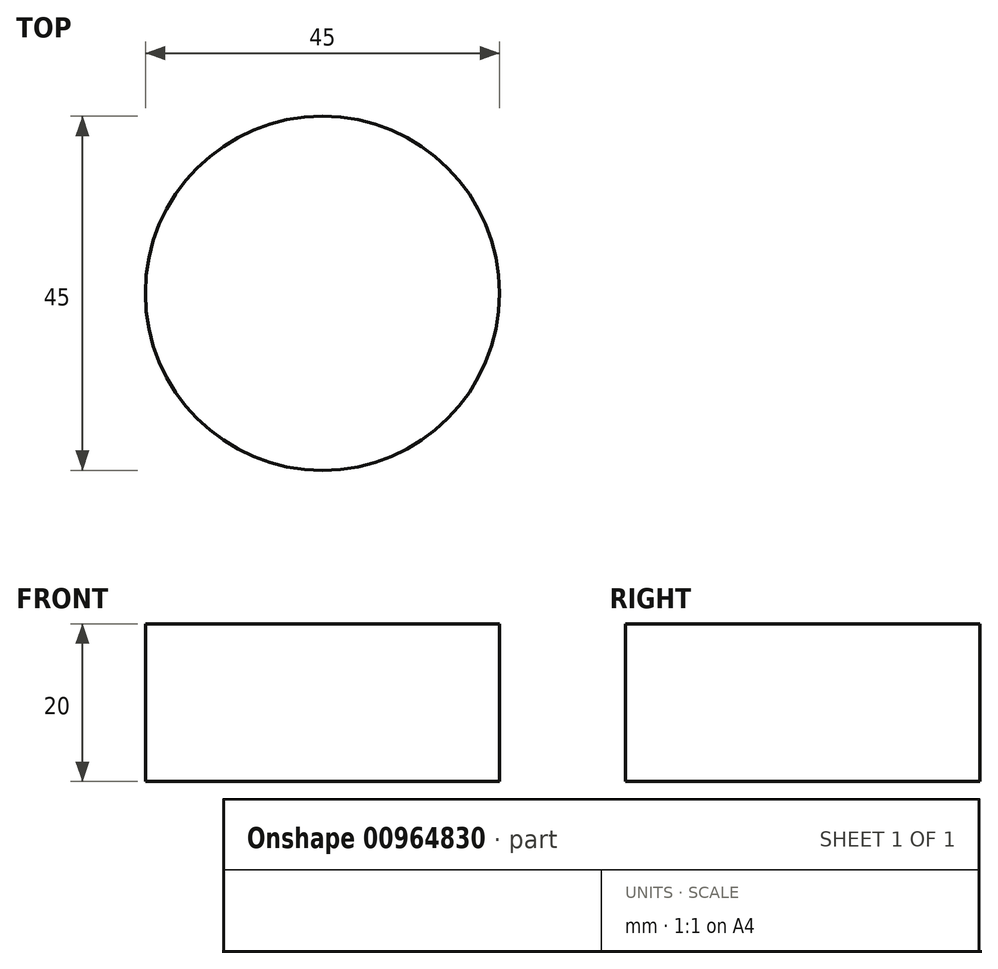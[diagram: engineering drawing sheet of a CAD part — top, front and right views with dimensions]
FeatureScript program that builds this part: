
annotation { "Feature Type Name" : "Feature", "Feature Type Description" : "" }
export const myFeature = defineFeature(function(context is Context, id is Id, definition is map)
    precondition{}
    {
        {
            var Q0;
            Q0=qCreatedBy(makeId("Top.planeOp"),FACE);
            var sketch = newSketch(context, id + "F0", { "sketchPlane" : qUnion([Q0])});
            skCircle(sketch, "E0", {"center": v(-35.7, 41.18) * mm, "radius": 22.5 * mm});
            skSolve(sketch);
        }
        {
            var Q0;
            Q0 = qSketchRegion(id + "F0", true);
            extrude(context, id + "F1", {"entities" : qUnion([Q0]), "depth" : 20 * mm, "offsetDistance" : 25 * mm});
        }
    });
